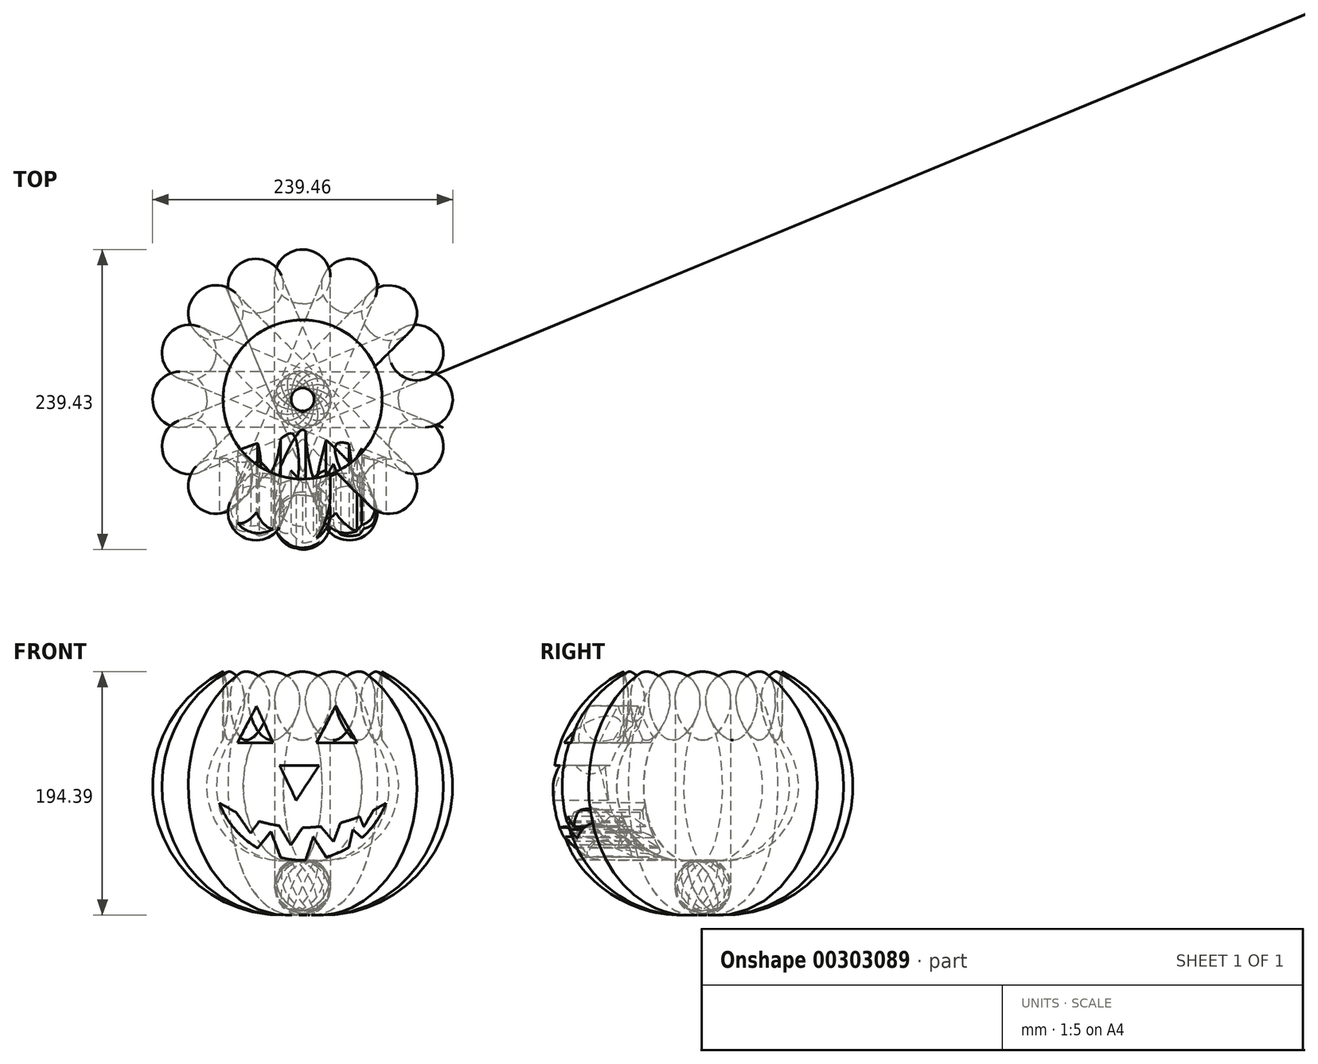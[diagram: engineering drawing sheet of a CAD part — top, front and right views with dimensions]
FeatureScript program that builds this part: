
annotation { "Feature Type Name" : "Feature", "Feature Type Description" : "" }
export const myFeature = defineFeature(function(context is Context, id is Id, definition is map)
    precondition{}
    {
        {
            var Q0;
            Q0=qCreatedBy(makeId("Front.planeOp"),FACE);
            var sketch = newSketch(context, id + "F0", { "sketchPlane" : qUnion([Q0])});
            skArc(sketch, "E0", {"start": v(0, 79.13) * mm, "mid": v(-97.9, 0) * mm, "end": v(0, -79.13) * mm});
            skPoint(sketch, "E1.center.orphan", {"position": v(0, 0) * mm});
            skPoint(sketch, "E1.end.orphan", {"position": v(0, -79.13) * mm});
            skSolve(sketch);
        }
        {
            var Q0;
            Q0=qCreatedBy(makeId("Right.planeOp"),FACE);
            var Q1;
            Q1=sQuery(id+"F0.wireOp",VERTEX,"E0.start");
            cPlane(context, id + "F1", {"entities" : qUnion([Q0, Q1]), "cplaneType" : CPlaneType.PLANE_POINT, "offset" : 25.4 * mm, "width" : 152.4 * mm, "height" : 152.4 * mm});
        }
        {
            var Q0;
            Q0=qCreatedBy(id+"F1.planeOp",FACE);
            var sketch = newSketch(context, id + "F2", { "sketchPlane" : qUnion([Q0])});
            skCircle(sketch, "E2", {"center": v(0, 79.13) * mm, "radius": 22.23 * mm});
            skCircle(sketch, "E3", {"center": v(0, -79.13) * mm, "radius": 22.23 * mm});
            skSolve(sketch);
        }
        {
            var Q0;
            Q0=makeQuery(id+"F2.imprint","IMPRINT",FACE,{"disambiguationData":[TD([[makeQuery(id+"F2.imprint","IMPRINT",EDGE,{"derivedFrom":sQuery(id+"F2.wireOp",EDGE,"E2")}),1.0]])]});
            var Q1;
            Q1=sQuery(id+"F0.wireOp",EDGE,"E0");
            sweep(context, id + "F3", {"profiles" : qUnion([Q0]), "path" : qUnion([Q1])});
        }
        {
            var Q0;
            Q0=qCreatedBy(id+"F1.planeOp",FACE);
            var sketch = newSketch(context, id + "F4", { "sketchPlane" : qUnion([Q0])});
            skLineSegment(sketch, "E4", {"start": v(0, -110.28) * mm, "end": v(0, 148.06) * mm});
            skSolve(sketch);
        }
        {
            var Q0;
            Q0=makeQuery(id+"F3.opSweep","SWEPT_BODY",BODY,{"disambiguationData":[OSD([sQuery(id+"F0.wireOp",EDGE,"E1"),sQuery(id+"F2.wireOp",EDGE,"E2")])]});
            var Q1;
            Q1=sQuery(id+"F4.wireOp",EDGE,"E4");
            circularPattern(context, id + "F5", {"entities" : qUnion([Q0]), "axis" : qUnion([Q1]), "angle" : 360 * degree, "instanceCount" : 16, "equalSpace" : true});
        }
        {
            var Q0;
            Q0=qCreatedBy(makeId("Top.planeOp"),FACE);
            cPlane(context, id + "F6", {"entities" : qUnion([Q0]), "cplaneType" : CPlaneType.OFFSET, "offset" : 127 * mm, "width" : 152.4 * mm, "height" : 152.4 * mm});
        }
        {
            var Q0;
            Q0=qCreatedBy(makeId("Front.planeOp"),FACE);
            cPlane(context, id + "F7", {"entities" : qUnion([Q0]), "cplaneType" : CPlaneType.OFFSET, "offset" : 127 * mm, "width" : 152.4 * mm, "height" : 152.4 * mm});
        }
        {
            var Q0;
            Q0=qCreatedBy(id+"F7.planeOp",FACE);
            var sketch = newSketch(context, id + "F8", { "sketchPlane" : qUnion([Q0])});
            skLineSegment(sketch, "E5", {"start": v(-51.98, 34.85) * mm, "end": v(-36.83, 64.12) * mm});
            skLineSegment(sketch, "E6", {"start": v(-36.83, 64.12) * mm, "end": v(-23.47, 34.85) * mm});
            skLineSegment(sketch, "E7", {"start": v(-23.47, 34.85) * mm, "end": v(-51.98, 34.85) * mm});
            skLineSegment(sketch, "E8", {"start": v(11.09, 34.85) * mm, "end": v(26.4, 64.43) * mm});
            skLineSegment(sketch, "E9", {"start": v(26.4, 64.43) * mm, "end": v(43.46, 34.85) * mm});
            skLineSegment(sketch, "E10", {"start": v(43.46, 34.85) * mm, "end": v(11.09, 34.85) * mm});
            skArc(sketch, "E11", {"start": v(-66.54, -13.16) * mm, "mid": v(-54.3, -33.82) * mm, "end": v(-35.89, -49.24) * mm});
            skLineSegment(sketch, "E12", {"start": v(-52.86, -20.82) * mm, "end": v(-41.52, -37.41) * mm});
            skLineSegment(sketch, "E13", {"start": v(-41.52, -37.41) * mm, "end": v(-34.68, -27.81) * mm});
            skLineSegment(sketch, "E14", {"start": v(-18.57, -31.41) * mm, "end": v(-9.45, -46.9) * mm});
            skLineSegment(sketch, "E15", {"start": v(-9.45, -46.9) * mm, "end": v(0, -32.83) * mm});
            skLineSegment(sketch, "E16", {"start": v(14.4, -31.98) * mm, "end": v(24.68, -44.08) * mm});
            skLineSegment(sketch, "E17", {"start": v(24.68, -44.08) * mm, "end": v(30.21, -29.04) * mm});
            skLineSegment(sketch, "E18", {"start": v(45.5, -24.06) * mm, "end": v(48.8, -32.28) * mm});
            skLineSegment(sketch, "E19", {"start": v(48.8, -32.28) * mm, "end": v(56.58, -18.96) * mm});
            skLineSegment(sketch, "E20", {"start": v(-35.89, -49.24) * mm, "end": v(-25.35, -36.13) * mm});
            skLineSegment(sketch, "E21", {"start": v(-25.35, -36.13) * mm, "end": v(-17.44, -56.78) * mm});
            skLineSegment(sketch, "E22", {"start": v(2.37, -58.9) * mm, "end": v(8.51, -40.23) * mm});
            skLineSegment(sketch, "E23", {"start": v(8.51, -40.23) * mm, "end": v(18.72, -56.44) * mm});
            skLineSegment(sketch, "E24", {"start": v(36.94, -48.62) * mm, "end": v(40.07, -34.33) * mm});
            skLineSegment(sketch, "E25", {"start": v(40.07, -34.33) * mm, "end": v(47.27, -41) * mm});
            skArc(sketch, "E26.trimOffspring", {"start": v(-34.68, -27.81) * mm, "mid": v(-26.68, -29.88) * mm, "end": v(-18.57, -31.41) * mm});
            skArc(sketch, "E27.trimOffspring", {"start": v(30.21, -29.04) * mm, "mid": v(37.94, -26.8) * mm, "end": v(45.5, -24.06) * mm});
            skArc(sketch, "E28.trimOffspring", {"start": v(0, -32.83) * mm, "mid": v(7.2, -32.62) * mm, "end": v(14.4, -31.98) * mm});
            skArc(sketch, "E29.trimOffspring", {"start": v(56.58, -18.96) * mm, "mid": v(61.63, -16.18) * mm, "end": v(66.54, -13.16) * mm});
            skArc(sketch, "E30.trimOffspring", {"start": v(47.27, -41) * mm, "mid": v(58.58, -28.24) * mm, "end": v(66.54, -13.16) * mm});
            skArc(sketch, "E31.trimOffspring", {"start": v(18.72, -56.44) * mm, "mid": v(28.1, -53.16) * mm, "end": v(36.94, -48.62) * mm});
            skArc(sketch, "E32.trimOffspring", {"start": v(-17.44, -56.78) * mm, "mid": v(-7.6, -58.53) * mm, "end": v(2.37, -58.9) * mm});
            skLineSegment(sketch, "E33", {"start": v(-52.86, -20.82) * mm, "end": v(-66.54, -13.16) * mm});
            skLineSegment(sketch, "E34", {"start": v(-5.13, -11.1) * mm, "end": v(-18.4, 16.8) * mm});
            skLineSegment(sketch, "E35", {"start": v(-18.4, 16.8) * mm, "end": v(13.18, 16.8) * mm});
            skLineSegment(sketch, "E36", {"start": v(13.18, 16.8) * mm, "end": v(-5.13, -11.1) * mm});
            skSolve(sketch);
        }
        {
            var Q0;
            Q0 = qSketchRegion(id + "F8", true);
            extrude(context, id + "F9", {"entities" : qUnion([Q0]), "operationType" : NewBodyOperationType.REMOVE, "oppositeDirection" : true, "depth" : 127 * mm});
        }
        {
            var Q0;
            Q0=qCreatedBy(id+"F6.planeOp",FACE);
            var sketch = newSketch(context, id + "F10", { "sketchPlane" : qUnion([Q0])});
            skCircle(sketch, "E37", {"center": v(0, 0) * mm, "radius": 63.5 * mm});
            skSolve(sketch);
        }
        {
            var Q0;
            Q0=makeQuery(id+"F10.imprint","IMPRINT",FACE,{"disambiguationData":[TD([[makeQuery(id+"F10.imprint","IMPRINT",EDGE,{"derivedFrom":sQuery(id+"F10.wireOp",EDGE,"E37")}),1.0]])]});
            extrude(context, id + "F11", {"entities" : qUnion([Q0]), "operationType" : NewBodyOperationType.REMOVE, "oppositeDirection" : true, "depth" : 101.6 * mm});
        }
    });
